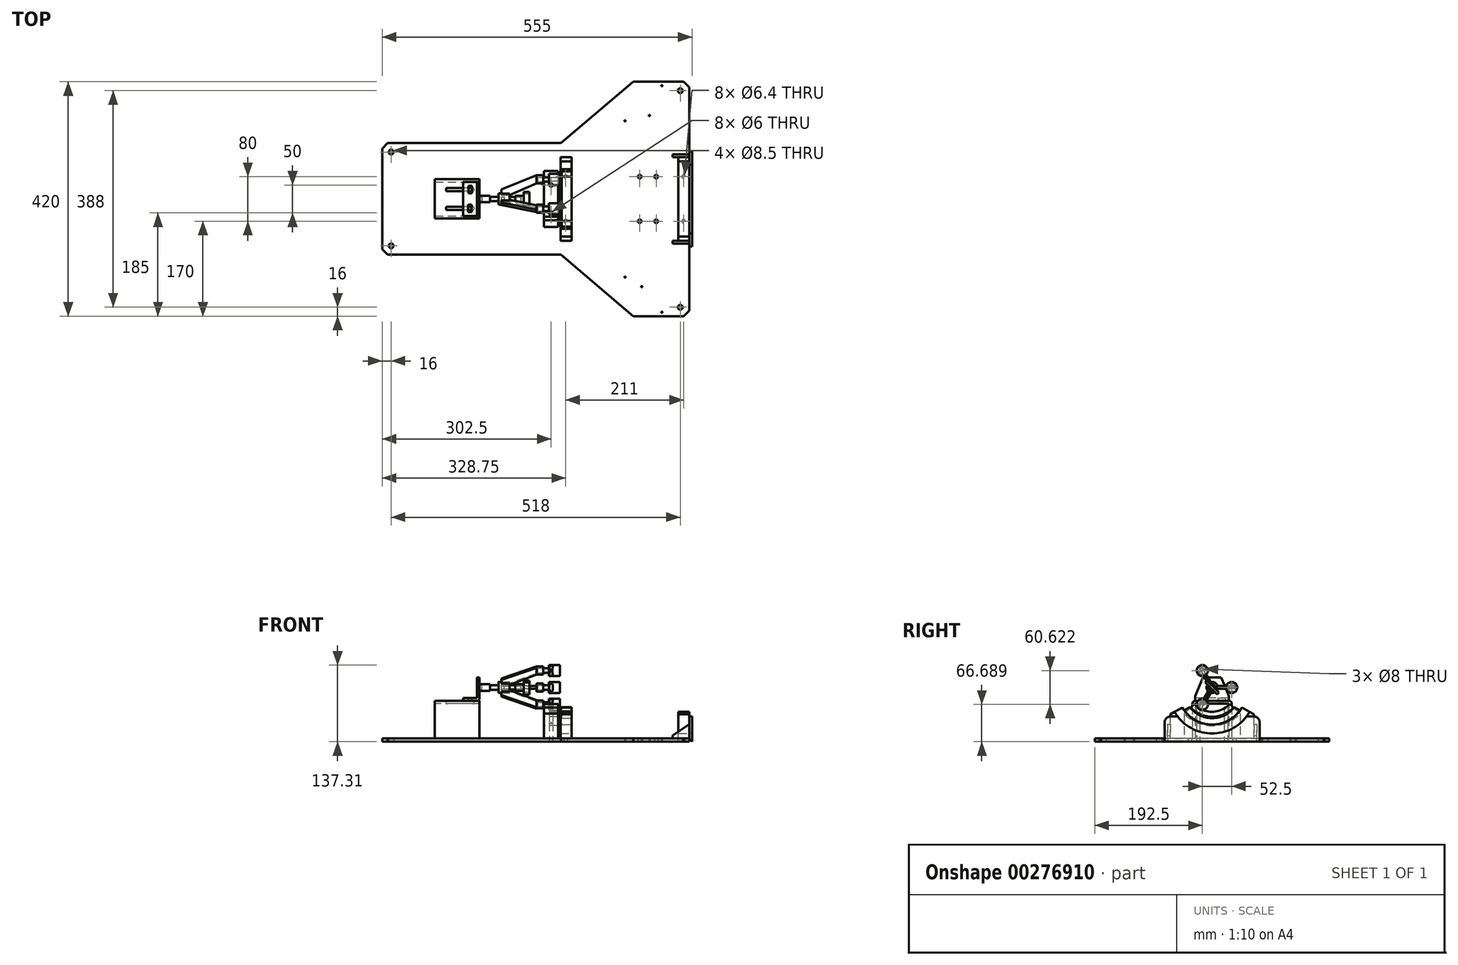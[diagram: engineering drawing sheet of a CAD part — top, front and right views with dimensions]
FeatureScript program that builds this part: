
annotation { "Feature Type Name" : "Feature", "Feature Type Description" : "" }
export const myFeature = defineFeature(function(context is Context, id is Id, definition is map)
    precondition{}
    {
        {
            var Q0;
            Q0=qCreatedBy(makeId("Top.planeOp"),FACE);
            var sketch = newSketch(context, id + "F0", { "sketchPlane" : qUnion([Q0])});
            skLineSegment(sketch, "E0.right", {"start": v(230, 200) * mm, "end": v(230, -200) * mm});
            skLineSegment(sketch, "E1", {"start": v(-320, 0) * mm, "end": v(230, 0) * mm, "construction": true});
            skCircle(sketch, "E2", {"center": v(8.75, 40) * mm, "radius": 3.2 * mm});
            skCircle(sketch, "E3", {"center": v(8.75, -40) * mm, "radius": 3.2 * mm});
            skCircle(sketch, "E4", {"center": v(115, -140) * mm, "radius": 1 * mm});
            skCircle(sketch, "E5", {"center": v(145, -157) * mm, "radius": 1 * mm});
            skCircle(sketch, "E6", {"center": v(181, -203) * mm, "radius": 1 * mm});
            skLineSegment(sketch, "E7", {"start": v(0, 0) * mm, "end": v(0, -188.14) * mm, "construction": true});
            skCircle(sketch, "E8", {"center": v(115, 140) * mm, "radius": 1 * mm});
            skCircle(sketch, "E9", {"center": v(158.66, 149.43) * mm, "radius": 1 * mm});
            skCircle(sketch, "E10", {"center": v(181, 203) * mm, "radius": 1 * mm});
            skLineSegment(sketch, "E11.0", {"start": v(-320, -50) * mm, "end": v(270, -50) * mm, "construction": true});
            skLineSegment(sketch, "E12.0", {"start": v(-320, 50) * mm, "end": v(270, 50) * mm, "construction": true});
            skLineSegment(sketch, "E13", {"start": v(-310, 100) * mm, "end": v(0, 100) * mm});
            skLineSegment(sketch, "E14", {"start": v(0, 100) * mm, "end": v(130, 210) * mm});
            skLineSegment(sketch, "E15", {"start": v(130, 210) * mm, "end": v(220, 210) * mm});
            skLineSegment(sketch, "E16", {"start": v(-310, -100) * mm, "end": v(0, -100) * mm});
            skLineSegment(sketch, "E17", {"start": v(0, -100) * mm, "end": v(130, -210) * mm});
            skLineSegment(sketch, "E18", {"start": v(-320, -90) * mm, "end": v(-320, 90) * mm});
            skLineSegment(sketch, "E19", {"start": v(130, -210) * mm, "end": v(220, -210) * mm});
            skLineSegment(sketch, "E20", {"start": v(8.75, 40) * mm, "end": v(230, 40) * mm, "construction": true});
            skCircle(sketch, "E21", {"center": v(141.25, 40) * mm, "radius": 3.2 * mm});
            skCircle(sketch, "E22", {"center": v(170.75, 40) * mm, "radius": 3.2 * mm});
            skCircle(sketch, "E23", {"center": v(219.75, 40) * mm, "radius": 3.2 * mm});
            skCircle(sketch, "E24", {"center": v(141.25, -40) * mm, "radius": 3.2 * mm});
            skCircle(sketch, "E25", {"center": v(170.75, -40) * mm, "radius": 3.2 * mm});
            skCircle(sketch, "E26", {"center": v(219.75, -40) * mm, "radius": 3.2 * mm});
            skLineSegment(sketch, "E27", {"start": v(-320, 90) * mm, "end": v(-310, 100) * mm});
            skLineSegment(sketch, "E28", {"start": v(-320, -90) * mm, "end": v(-310, -100) * mm});
            skLineSegment(sketch, "E29", {"start": v(220, -210) * mm, "end": v(230, -200) * mm});
            skLineSegment(sketch, "E30", {"start": v(220, 210) * mm, "end": v(230, 200) * mm});
            skPoint(sketch, "E31.orphan", {"position": v(-320, 100) * mm});
            skPoint(sketch, "E32.orphan", {"position": v(-320, -100) * mm});
            skPoint(sketch, "E33.orphan", {"position": v(230, -210) * mm});
            skPoint(sketch, "E34.orphan", {"position": v(230, 210) * mm});
            skSolve(sketch);
        }
        {
            var Q0;
            Q0=makeQuery(id+"F0.imprint","IMPRINT",FACE,{"disambiguationData":[TD([[makeQuery(id+"F0.imprint","IMPRINT",EDGE,{"derivedFrom":sQuery(id+"F0.wireOp",EDGE,"E0.right")}),-1.0]])]});
            extrude(context, id + "F1", {"entities" : qUnion([Q0]), "depth" : 6 * mm});
        }
        {
            var Q0;
            Q0=makeQuery(id+"F1.opExtrude","CAP_FACE",FACE,{"disambiguationData":[OSD([sQuery(id+"F0.wireOp",EDGE,"E0.right"),sQuery(id+"F0.wireOp",EDGE,"E2"),sQuery(id+"F0.wireOp",EDGE,"E3"),sQuery(id+"F0.wireOp",EDGE,"E4"),sQuery(id+"F0.wireOp",EDGE,"E5"),sQuery(id+"F0.wireOp",EDGE,"E6"),sQuery(id+"F0.wireOp",EDGE,"E8"),sQuery(id+"F0.wireOp",EDGE,"E9"),sQuery(id+"F0.wireOp",EDGE,"E10"),sQuery(id+"F0.wireOp",EDGE,"E13"),sQuery(id+"F0.wireOp",EDGE,"E14"),sQuery(id+"F0.wireOp",EDGE,"E15"),sQuery(id+"F0.wireOp",EDGE,"E16"),sQuery(id+"F0.wireOp",EDGE,"E17"),sQuery(id+"F0.wireOp",EDGE,"E18"),sQuery(id+"F0.wireOp",EDGE,"E19"),sQuery(id+"F0.wireOp",EDGE,"E21"),sQuery(id+"F0.wireOp",EDGE,"E22"),sQuery(id+"F0.wireOp",EDGE,"E23"),sQuery(id+"F0.wireOp",EDGE,"E24"),sQuery(id+"F0.wireOp",EDGE,"E25"),sQuery(id+"F0.wireOp",EDGE,"E26"),sQuery(id+"F0.wireOp",EDGE,"E27"),sQuery(id+"F0.wireOp",EDGE,"E28"),sQuery(id+"F0.wireOp",EDGE,"E29"),sQuery(id+"F0.wireOp",EDGE,"E30")])],"isStart":false});
            cPlane(context, id + "F2", {"entities" : qUnion([Q0]), "cplaneType" : CPlaneType.OFFSET, "offset" : 67 * mm, "width" : 150 * mm, "height" : 150 * mm});
        }
        {
            var Q0;
            Q0=qCreatedBy(id+"F2.planeOp",FACE);
            var sketch = newSketch(context, id + "F3", { "sketchPlane" : qUnion([Q0])});
            skLineSegment(sketch, "E35.bottom", {"start": v(-175.1, 30.25) * mm, "end": v(-145.6, 30.25) * mm});
            skLineSegment(sketch, "E35.top", {"start": v(-175.1, -30.25) * mm, "end": v(-145.6, -30.25) * mm});
            skLineSegment(sketch, "E35.left", {"start": v(-175.1, 30.25) * mm, "end": v(-175.1, -30.25) * mm});
            skLineSegment(sketch, "E35.right", {"start": v(-145.6, 30.25) * mm, "end": v(-145.6, -30.25) * mm});
            skLineSegment(sketch, "E36", {"start": v(0, 0) * mm, "end": v(-175.1, 0) * mm, "construction": true});
            skLineSegment(sketch, "E37.bottom", {"start": v(-166.1, -23.38) * mm, "end": v(-160.1, -23.38) * mm});
            skLineSegment(sketch, "E37.top", {"start": v(-166.1, -10.38) * mm, "end": v(-160.1, -10.38) * mm});
            skLineSegment(sketch, "E37.left", {"start": v(-166.1, -23.38) * mm, "end": v(-166.1, -10.38) * mm});
            skLineSegment(sketch, "E37.right", {"start": v(-160.1, -23.38) * mm, "end": v(-160.1, -10.38) * mm});
            skLineSegment(sketch, "E38.bottom", {"start": v(-165.48, 10.38) * mm, "end": v(-159.48, 10.38) * mm});
            skLineSegment(sketch, "E38.top", {"start": v(-165.48, 23.38) * mm, "end": v(-159.48, 23.38) * mm});
            skLineSegment(sketch, "E38.left", {"start": v(-165.48, 10.38) * mm, "end": v(-165.48, 23.38) * mm});
            skLineSegment(sketch, "E38.right", {"start": v(-159.48, 10.38) * mm, "end": v(-159.48, 23.38) * mm});
            skSolve(sketch);
        }
        {
            var Q0;
            Q0=makeQuery(id+"F3.imprint","IMPRINT",FACE,{"disambiguationData":[TD([[makeQuery(id+"F3.imprint","IMPRINT",EDGE,{"derivedFrom":sQuery(id+"F3.wireOp",EDGE,"E35.bottom")}),-1.0]])]});
            extrude(context, id + "F4", {"entities" : qUnion([Q0]), "depth" : 5 * mm});
        }
        {
            var Q0;
            Q0=makeQuery(id+"F4.opExtrude","SWEPT_FACE",FACE,{"disambiguationData":[OSD([sQuery(id+"F3.wireOp",EDGE,"E35.right")])]});
            var sketch = newSketch(context, id + "F5", { "sketchPlane" : qUnion([Q0])});
            skLineSegment(sketch, "E39.0", {"start": v(30.25, 73) * mm, "end": v(-30.25, 73) * mm});
            skLineSegment(sketch, "E39.1", {"start": v(-30.25, 78) * mm, "end": v(-30.25, 73) * mm});
            skLineSegment(sketch, "E39.2", {"start": v(30.25, 78) * mm, "end": v(30.25, 73) * mm});
            skLineSegment(sketch, "E40", {"start": v(-30.25, 78) * mm, "end": v(-30.25, 81.7) * mm});
            skLineSegment(sketch, "E41", {"start": v(-30.25, 81.7) * mm, "end": v(-16.23, 115) * mm});
            skLineSegment(sketch, "E42", {"start": v(-16.23, 115) * mm, "end": v(16.23, 115) * mm});
            skLineSegment(sketch, "E43", {"start": v(16.23, 115) * mm, "end": v(30.25, 81.7) * mm});
            skLineSegment(sketch, "E44", {"start": v(30.25, 81.7) * mm, "end": v(30.25, 78) * mm});
            skLineSegment(sketch, "E45", {"start": v(0, 115) * mm, "end": v(0, 78) * mm, "construction": true});
            skCircle(sketch, "E46", {"center": v(0, 97) * mm, "radius": 6 * mm, "construction": true});
            skSolve(sketch);
        }
        {
            var Q0;
            Q0=makeQuery(id+"F5.imprint","IMPRINT",FACE,{"disambiguationData":[TD([[makeQuery(id+"F5.imprint","IMPRINT",EDGE,{"derivedFrom":sQuery(id+"F5.wireOp",EDGE,"E40")}),-1.0]])]});
            extrude(context, id + "F6", {"entities" : qUnion([Q0]), "operationType" : NewBodyOperationType.ADD, "oppositeDirection" : true, "depth" : 5 * mm});
        }
        {
            var Q0;
            Q0=makeQuery(id+"F4.opExtrude","CAP_EDGE",EDGE,{"disambiguationData":[OSD([sQuery(id+"F3.wireOp",EDGE,"E35.right")])],"isStart":true});
            fillet(context, id + "F7", {"entities" : qUnion([Q0]), "radius" : 5 * mm, "tangentPropagation" : true, "allowEdgeOverflow" : false});
        }
        {
            var Q0;
            Q0=makeQuery(id+"F5.imprint","IMPRINT",FACE,{"disambiguationData":[TD([[makeQuery(id+"F5.imprint","IMPRINT",EDGE,{"derivedFrom":sQuery(id+"F5.wireOp",EDGE,"E40")}),-1.0]])]});
            var sketch = newSketch(context, id + "F8", { "sketchPlane" : qUnion([Q0])});
            skCircle(sketch, "E47.0", {"center": v(0, 97) * mm, "radius": 6 * mm});
            skCircle(sketch, "E48", {"center": v(0, 97) * mm, "radius": 4 * mm});
            skSolve(sketch);
        }
        {
            var Q0;
            Q0=makeQuery(id+"F8.imprint","IMPRINT",FACE,{"disambiguationData":[TD([[makeQuery(id+"F8.imprint","IMPRINT",EDGE,{"derivedFrom":sQuery(id+"F8.wireOp",EDGE,"E47.0")}),1.0]])]});
            var Q1;
            Q1=sQuery(id+"F8.wireOp",EDGE,"E47.0");
            extrude(context, id + "F9", {"entities" : qUnion([Q0]), "surfaceEntities" : qUnion([Q1]), "depth" : 19 * mm});
        }
        {
            var Q0;
            Q0=makeQuery(id+"F9.opExtrude","CAP_FACE",FACE,{"disambiguationData":[OSD([sQuery(id+"F8.wireOp",EDGE,"E47.0"),sQuery(id+"F8.wireOp",EDGE,"E48")])],"isStart":false});
            var sketch = newSketch(context, id + "F10", { "sketchPlane" : qUnion([Q0])});
            skCircle(sketch, "E49.0", {"center": v(0, 97) * mm, "radius": 4 * mm});
            skSolve(sketch);
        }
        {
            var Q0;
            Q0=makeQuery(id+"F10.imprint","IMPRINT",FACE,{"disambiguationData":[TD([[makeQuery(id+"F10.imprint","IMPRINT",EDGE,{"derivedFrom":sQuery(id+"F10.wireOp",EDGE,"E49.0")}),1.0]])]});
            extrude(context, id + "F11", {"entities" : qUnion([Q0]), "oppositeDirection" : true, "depth" : 15 * mm});
        }
        {
            var Q0;
            Q0=makeQuery(id+"F11.opExtrude","CAP_FACE",FACE,{"disambiguationData":[OSD([sQuery(id+"F10.wireOp",EDGE,"E49.0")])],"isStart":true});
            extrude(context, id + "F12", {"entities" : qUnion([Q0]), "operationType" : NewBodyOperationType.ADD, "depth" : 15 * mm});
        }
        {
            var Q0;
            Q0=makeQuery(id+"F12.opExtrude","CAP_FACE",FACE,{"disambiguationData":[OSD([sQuery(id+"F10.wireOp",EDGE,"E49.0")])],"isStart":false});
            var sketch = newSketch(context, id + "F13", { "sketchPlane" : qUnion([Q0])});
            skCircle(sketch, "E50", {"center": v(0, 97) * mm, "radius": 10 * mm});
            skSolve(sketch);
        }
        {
            var Q0;
            Q0=makeQuery(id+"F13.imprint","IMPRINT",FACE,{"disambiguationData":[TD([[makeQuery(id+"F13.imprint","IMPRINT",EDGE,{"derivedFrom":sQuery(id+"F13.wireOp",EDGE,"E50")}),1.0]])]});
            var Q1;
            Q1=makeQuery(id+"F13.imprint","IMPRINT",FACE,{"disambiguationData":[TD([[makeQuery(id+"F13.imprint","IMPRINT",EDGE,{"derivedFrom":makeQuery(id+"F12.opExtrude","CAP_EDGE",EDGE,{"disambiguationData":[OSD([sQuery(id+"F10.wireOp",EDGE,"E49.0")])],"isStart":false})}),1.0]])]});
            extrude(context, id + "F14", {"entities" : qUnion([Q0, Q1]), "operationType" : NewBodyOperationType.ADD, "depth" : 20 * mm});
        }
        {
            var Q0;
            Q0=makeQuery(id+"F14.opExtrude","CAP_FACE",FACE,{"disambiguationData":[OSD([sQuery(id+"F13.wireOp",EDGE,"E50")])],"isStart":false});
            var sketch = newSketch(context, id + "F15", { "sketchPlane" : qUnion([Q0])});
            skCircle(sketch, "E51", {"center": v(0, 97) * mm, "radius": 4 * mm});
            skLineSegment(sketch, "E52", {"start": v(0, 97) * mm, "end": v(10, 97) * mm, "construction": true});
            skLineSegment(sketch, "E53", {"start": v(0, 97) * mm, "end": v(-5, 88.34) * mm, "construction": true});
            skLineSegment(sketch, "E54", {"start": v(0, 97) * mm, "end": v(-5, 105.66) * mm, "construction": true});
            skLineSegment(sketch, "E55", {"start": v(9.68, 94.5) * mm, "end": v(7, 94.5) * mm});
            skLineSegment(sketch, "E56", {"start": v(7, 94.5) * mm, "end": v(7, 99.5) * mm});
            skLineSegment(sketch, "E57", {"start": v(7, 99.5) * mm, "end": v(9.68, 99.5) * mm});
            skLineSegment(sketch, "E58", {"start": v(-7, 89.86) * mm, "end": v(-5.67, 92.19) * mm});
            skLineSegment(sketch, "E59", {"start": v(-5.67, 92.19) * mm, "end": v(-1.33, 89.69) * mm});
            skLineSegment(sketch, "E60", {"start": v(-1.33, 89.69) * mm, "end": v(-2.68, 87.36) * mm});
            skLineSegment(sketch, "E61", {"start": v(-2.68, 106.64) * mm, "end": v(-1.33, 104.31) * mm});
            skLineSegment(sketch, "E62", {"start": v(-1.33, 104.31) * mm, "end": v(-5.67, 101.81) * mm});
            skLineSegment(sketch, "E63", {"start": v(-5.67, 101.81) * mm, "end": v(-7, 104.14) * mm});
            skSolve(sketch);
        }
        {
            var Q0;
            Q0=makeQuery(id+"F15.imprint","IMPRINT",FACE,{"disambiguationData":[TD([[makeQuery(id+"F15.imprint","IMPRINT",EDGE,{"derivedFrom":sQuery(id+"F15.wireOp",EDGE,"E51")}),1.0]])]});
            extrude(context, id + "F16", {"entities" : qUnion([Q0]), "operationType" : NewBodyOperationType.REMOVE, "oppositeDirection" : true, "depth" : 15 * mm});
        }
        {
            var Q0;
            {var subQ0=sQuery(id+"F15.wireOp",EDGE,"E61");Q0=makeQuery(id+"F15.imprint","IMPRINT",FACE,{"disambiguationData":[TD([[makeQuery(id+"F15.imprint","IMPRINT",EDGE,{"derivedFrom":subQ0}),-1.0]])]});}
            var Q1;
            {var subQ0=sQuery(id+"F15.wireOp",EDGE,"E58");Q1=makeQuery(id+"F15.imprint","IMPRINT",FACE,{"disambiguationData":[TD([[makeQuery(id+"F15.imprint","IMPRINT",EDGE,{"derivedFrom":subQ0}),-1.0]])]});}
            var Q2;
            {var subQ0=sQuery(id+"F15.wireOp",EDGE,"E55");Q2=makeQuery(id+"F15.imprint","IMPRINT",FACE,{"disambiguationData":[TD([[makeQuery(id+"F15.imprint","IMPRINT",EDGE,{"derivedFrom":subQ0}),-1.0]])]});}
            extrude(context, id + "F17", {"entities" : qUnion([Q0, Q1, Q2]), "operationType" : NewBodyOperationType.REMOVE, "oppositeDirection" : true, "depth" : 15 * mm});
        }
        {
            var Q0;
            Q0=makeQuery(id+"F14.opExtrude","CAP_FACE",FACE,{"disambiguationData":[OSD([sQuery(id+"F13.wireOp",EDGE,"E50")])],"isStart":false});
            var sketch = newSketch(context, id + "F18", { "sketchPlane" : qUnion([Q0])});
            skCircle(sketch, "E64", {"center": v(0, 97) * mm, "radius": 4 * mm});
            skSolve(sketch);
        }
        {
            var Q0;
            Q0=makeQuery(id+"F18.imprint","IMPRINT",FACE,{"disambiguationData":[TD([[makeQuery(id+"F18.imprint","IMPRINT",EDGE,{"derivedFrom":sQuery(id+"F18.wireOp",EDGE,"E64")}),1.0]])]});
            extrude(context, id + "F19", {"entities" : qUnion([Q0]), "oppositeDirection" : true, "depth" : 10 * mm});
        }
        {
            var Q0;
            Q0=makeQuery(id+"F19.opExtrude","CAP_FACE",FACE,{"disambiguationData":[OSD([sQuery(id+"F18.wireOp",EDGE,"E64")])],"isStart":true});
            extrude(context, id + "F20", {"entities" : qUnion([Q0]), "operationType" : NewBodyOperationType.ADD, "depth" : 20 * mm});
        }
        {
            var Q0;
            Q0=makeQuery(id+"F20.opExtrude","CAP_FACE",FACE,{"disambiguationData":[OSD([sQuery(id+"F18.wireOp",EDGE,"E64")])],"isStart":false});
            cPlane(context, id + "F21", {"entities" : qUnion([Q0]), "cplaneType" : CPlaneType.OFFSET, "offset" : 10 * mm, "oppositeDirection" : true, "width" : 150 * mm, "height" : 150 * mm});
        }
        {
            var Q0;
            Q0=qCreatedBy(id+"F21.planeOp",FACE);
            var sketch = newSketch(context, id + "F22", { "sketchPlane" : qUnion([Q0])});
            skLineSegment(sketch, "E65.0", {"start": v(0, 115) * mm, "end": v(0, 78) * mm, "construction": true});
            skCircle(sketch, "E66.0", {"center": v(0, 97) * mm, "radius": 4 * mm, "construction": true});
            skCircle(sketch, "E67", {"center": v(0, 97) * mm, "radius": 6 * mm});
            skSolve(sketch);
        }
        {
            var Q0;
            Q0=makeQuery(id+"F22.imprint","IMPRINT",FACE,{"disambiguationData":[TD([[makeQuery(id+"F22.imprint","IMPRINT",EDGE,{"derivedFrom":sQuery(id+"F22.wireOp",EDGE,"E67")}),1.0]])]});
            extrude(context, id + "F23", {"entities" : qUnion([Q0]), "depth" : 15 * mm});
        }
        {
            var Q0;
            Q0=makeQuery(id+"F23.opExtrude","CAP_FACE",FACE,{"disambiguationData":[OSD([sQuery(id+"F22.wireOp",EDGE,"E67")])],"isStart":false});
            var sketch = newSketch(context, id + "F24", { "sketchPlane" : qUnion([Q0])});
            skLineSegment(sketch, "E68", {"start": v(0, 103) * mm, "end": v(0, 91) * mm, "construction": true});
            skLineSegment(sketch, "E69.bottom", {"start": v(-2.5, 112) * mm, "end": v(2.5, 112) * mm});
            skLineSegment(sketch, "E69.top", {"start": v(-2.5, 82) * mm, "end": v(2.5, 82) * mm});
            skLineSegment(sketch, "E69.left", {"start": v(-2.5, 112) * mm, "end": v(-2.5, 82) * mm});
            skLineSegment(sketch, "E69.right", {"start": v(2.5, 112) * mm, "end": v(2.5, 82) * mm});
            skLineSegment(sketch, "E70", {"start": v(0, 97) * mm, "end": v(2.5, 97) * mm, "construction": true});
            skSolve(sketch);
        }
        {
            var Q0;
            {var subQ0=sQuery(id+"F24.wireOp",EDGE,"E69.bottom");Q0=makeQuery(id+"F24.imprint","IMPRINT",FACE,{"disambiguationData":[TD([[makeQuery(id+"F24.imprint","IMPRINT",EDGE,{"derivedFrom":subQ0}),-1.0]])]});}
            var Q1;
            {var subQ0=sQuery(id+"F24.wireOp",EDGE,"E69.left");var subQ1=makeQuery(id+"F23.opExtrude","CAP_EDGE",EDGE,{"disambiguationData":[OSD([sQuery(id+"F22.wireOp",EDGE,"E67")])],"isStart":false});var subQ2=makeQuery(id+"F24.imprint","INTERSECT",VERTEX,{"disambiguationData":[OD(0.0)],"derivedFrom":[subQ1,subQ0]});Q1=makeQuery(id+"F24.imprint","IMPRINT",FACE,{"disambiguationData":[TD([[makeQuery(id+"F24.imprint","IMPRINT",EDGE,{"disambiguationData":[TD([[subQ2,-1.0]])],"derivedFrom":subQ0}),1.0]])]});}
            var Q2;
            {var subQ0=sQuery(id+"F24.wireOp",EDGE,"E69.top");Q2=makeQuery(id+"F24.imprint","IMPRINT",FACE,{"disambiguationData":[TD([[makeQuery(id+"F24.imprint","IMPRINT",EDGE,{"derivedFrom":subQ0}),1.0]])]});}
            extrude(context, id + "F25", {"entities" : qUnion([Q0, Q1, Q2]), "operationType" : NewBodyOperationType.ADD, "depth" : 10 * mm});
        }
        {
            var Q0;
            Q0=makeQuery(id+"F23.opExtrude","SWEPT_BODY",BODY,{"disambiguationData":[OSD([sQuery(id+"F22.wireOp",EDGE,"E67")])]});
            var Q1;
            {var subQ0=sQuery(id+"F18.wireOp",EDGE,"E64");Q1=makeQuery(id+"F20.boolean.opBoolean","MERGE",FACE,{"derivedFrom":[makeQuery(id+"F19.opExtrude","SWEPT_FACE",FACE,{"disambiguationData":[OSD([subQ0])]}),makeQuery(id+"F20.opExtrude","SWEPT_FACE",FACE,{"disambiguationData":[OSD([subQ0])]})]});}
            transform(context, id + "F26", {"entities" : qUnion([Q0]), "transformType" : TransformType.ROTATION, "transformAxis" : qUnion([Q1]), "angle" : 45 * degree, "makeCopy" : false});
        }
        {
            var Q0;
            Q0=makeQuery(id+"F25.opExtrude","CAP_FACE",FACE,{"disambiguationData":[OSD([sQuery(id+"F24.wireOp",EDGE,"E69.bottom"),sQuery(id+"F24.wireOp",EDGE,"E69.top"),sQuery(id+"F24.wireOp",EDGE,"E69.left"),sQuery(id+"F24.wireOp",EDGE,"E69.right")])],"isStart":false});
            cPlane(context, id + "F27", {"entities" : qUnion([Q0]), "cplaneType" : CPlaneType.OFFSET, "offset" : 55 * mm, "width" : 150 * mm, "height" : 150 * mm});
        }
        {
            var Q0;
            Q0=qCreatedBy(id+"F27.planeOp",FACE);
            var sketch = newSketch(context, id + "F28", { "sketchPlane" : qUnion([Q0])});
            skCircle(sketch, "E71", {"center": v(0, 97) * mm, "radius": 43.5 * mm, "construction": true});
            skCircle(sketch, "E72", {"center": v(0, 97) * mm, "radius": 35 * mm, "construction": true});
            skLineSegment(sketch, "E73", {"start": v(0, 97) * mm, "end": v(43.5, 97) * mm, "construction": true});
            skLineSegment(sketch, "E74", {"start": v(0, 97) * mm, "end": v(-21.75, 59.33) * mm, "construction": true});
            skLineSegment(sketch, "E75", {"start": v(0, 97) * mm, "end": v(-21.75, 134.67) * mm, "construction": true});
            skCircle(sketch, "E76", {"center": v(-17.5, 66.69) * mm, "radius": 10 * mm});
            skCircle(sketch, "E77", {"center": v(35, 97) * mm, "radius": 10 * mm});
            skCircle(sketch, "E78", {"center": v(-17.5, 127.31) * mm, "radius": 10 * mm});
            skSolve(sketch);
        }
        {
            var Q0;
            Q0=makeQuery(id+"F28.imprint","IMPRINT",FACE,{"disambiguationData":[TD([[makeQuery(id+"F28.imprint","IMPRINT",EDGE,{"derivedFrom":sQuery(id+"F28.wireOp",EDGE,"E78")}),1.0]])]});
            var Q1;
            Q1=makeQuery(id+"F28.imprint","IMPRINT",FACE,{"disambiguationData":[TD([[makeQuery(id+"F28.imprint","IMPRINT",EDGE,{"derivedFrom":sQuery(id+"F28.wireOp",EDGE,"E77")}),1.0]])]});
            var Q2;
            Q2=makeQuery(id+"F28.imprint","IMPRINT",FACE,{"disambiguationData":[TD([[makeQuery(id+"F28.imprint","IMPRINT",EDGE,{"derivedFrom":sQuery(id+"F28.wireOp",EDGE,"E76")}),1.0]])]});
            extrude(context, id + "F29", {"entities" : qUnion([Q0, Q1, Q2]), "oppositeDirection" : true, "depth" : 20 * mm});
        }
        {
            var Q0;
            Q0=makeQuery(id+"F29.opExtrude","CAP_FACE",FACE,{"disambiguationData":[OSD([sQuery(id+"F28.wireOp",EDGE,"E78")])],"isStart":false});
            var sketch = newSketch(context, id + "F30", { "sketchPlane" : qUnion([Q0])});
            skCircle(sketch, "E79", {"center": v(17.5, 127.31) * mm, "radius": 4 * mm});
            skCircle(sketch, "E80", {"center": v(17.5, 66.69) * mm, "radius": 4 * mm});
            skCircle(sketch, "E81", {"center": v(-35, 97) * mm, "radius": 4 * mm});
            skSolve(sketch);
        }
        {
            var Q0;
            Q0=makeQuery(id+"F30.imprint","IMPRINT",FACE,{"disambiguationData":[TD([[makeQuery(id+"F30.imprint","IMPRINT",EDGE,{"derivedFrom":sQuery(id+"F30.wireOp",EDGE,"E80")}),1.0]])]});
            var Q1;
            Q1=makeQuery(id+"F30.imprint","IMPRINT",FACE,{"disambiguationData":[TD([[makeQuery(id+"F30.imprint","IMPRINT",EDGE,{"derivedFrom":sQuery(id+"F30.wireOp",EDGE,"E81")}),1.0]])]});
            var Q2;
            Q2=makeQuery(id+"F30.imprint","IMPRINT",FACE,{"disambiguationData":[TD([[makeQuery(id+"F30.imprint","IMPRINT",EDGE,{"derivedFrom":sQuery(id+"F30.wireOp",EDGE,"E79")}),1.0]])]});
            extrude(context, id + "F31", {"entities" : qUnion([Q0, Q1, Q2]), "depth" : 20 * mm});
        }
        {
            var Q0;
            Q0=makeQuery(id+"F31.opExtrude","CAP_FACE",FACE,{"disambiguationData":[OSD([sQuery(id+"F30.wireOp",EDGE,"E79")])],"isStart":false});
            cPlane(context, id + "F32", {"entities" : qUnion([Q0]), "cplaneType" : CPlaneType.OFFSET, "offset" : 10 * mm, "oppositeDirection" : true, "width" : 150 * mm, "height" : 150 * mm});
        }
        {
            var Q0;
            Q0=qCreatedBy(id+"F32.planeOp",FACE);
            var sketch = newSketch(context, id + "F33", { "sketchPlane" : qUnion([Q0])});
            skCircle(sketch, "E82.0", {"center": v(17.5, 127.31) * mm, "radius": 4 * mm});
            skCircle(sketch, "E82.1", {"center": v(-35, 97) * mm, "radius": 4 * mm});
            skCircle(sketch, "E82.2", {"center": v(17.5, 66.69) * mm, "radius": 4 * mm});
            skCircle(sketch, "E83", {"center": v(17.5, 127.31) * mm, "radius": 7.2 * mm});
            skCircle(sketch, "E84", {"center": v(-35, 97) * mm, "radius": 7.2 * mm});
            skCircle(sketch, "E85", {"center": v(17.5, 66.69) * mm, "radius": 7.2 * mm});
            skSolve(sketch);
        }
        {
            var Q0;
            Q0=makeQuery(id+"F33.imprint","IMPRINT",FACE,{"disambiguationData":[TD([[makeQuery(id+"F33.imprint","IMPRINT",EDGE,{"derivedFrom":sQuery(id+"F33.wireOp",EDGE,"E82.0")}),-1.0]])]});
            var Q1;
            Q1=makeQuery(id+"F33.imprint","IMPRINT",FACE,{"disambiguationData":[TD([[makeQuery(id+"F33.imprint","IMPRINT",EDGE,{"derivedFrom":sQuery(id+"F33.wireOp",EDGE,"E82.2")}),-1.0]])]});
            var Q2;
            Q2=makeQuery(id+"F33.imprint","IMPRINT",FACE,{"disambiguationData":[TD([[makeQuery(id+"F33.imprint","IMPRINT",EDGE,{"derivedFrom":sQuery(id+"F33.wireOp",EDGE,"E82.1")}),-1.0]])]});
            extrude(context, id + "F34", {"entities" : qUnion([Q0, Q1, Q2]), "depth" : 12 * mm});
        }
        {
            var Q0;
            Q0=makeQuery(id+"F17.boolean.opBoolean","COPY",FACE,{"derivedFrom":makeQuery(id+"F17.opExtrude","SWEPT_FACE",FACE,{"disambiguationData":[OSD([sQuery(id+"F15.wireOp",EDGE,"E63")])]})});
            var sketch = newSketch(context, id + "F35", { "sketchPlane" : qUnion([Q0])});
            skLineSegment(sketch, "E86.0", {"start": v(106.6, 91) * mm, "end": v(91.6, 91) * mm});
            skLineSegment(sketch, "E87.0", {"start": v(106.6, 93.69) * mm, "end": v(106.6, 91) * mm});
            skLineSegment(sketch, "E88", {"start": v(106.6, 93.69) * mm, "end": v(106.6, 101) * mm});
            skLineSegment(sketch, "E89", {"start": v(106.6, 101) * mm, "end": v(43.6, 126.2) * mm});
            skLineSegment(sketch, "E90.0", {"start": v(43.6, 126.2) * mm, "end": v(43.6, 111.8) * mm});
            skLineSegment(sketch, "E91", {"start": v(43.6, 111.8) * mm, "end": v(91.6, 91) * mm});
            skSolve(sketch);
        }
        {
            var Q0;
            Q0=makeQuery(id+"F35.imprint","IMPRINT",FACE,{"disambiguationData":[TD([[makeQuery(id+"F35.imprint","IMPRINT",EDGE,{"derivedFrom":sQuery(id+"F35.wireOp",EDGE,"E88")}),1.0]])]});
            var Q1;
            Q1=makeQuery(id+"F35.imprint","IMPRINT",FACE,{"disambiguationData":[TD([[makeQuery(id+"F35.imprint","IMPRINT",EDGE,{"derivedFrom":sQuery(id+"F35.wireOp",EDGE,"E86.0")}),-1.0]])]});
            extrude(context, id + "F36", {"entities" : qUnion([Q0, Q1]), "depth" : 5 * mm});
        }
        {
            var Q0;
            Q0=makeQuery(id+"F36.opExtrude","SWEPT_BODY",BODY,{"disambiguationData":[OSD([sQuery(id+"F13.wireOp",EDGE,"E50"),sQuery(id+"F15.wireOp",EDGE,"E63"),sQuery(id+"F35.wireOp",EDGE,"E88"),sQuery(id+"F35.wireOp",EDGE,"E89"),sQuery(id+"F35.wireOp",EDGE,"E90.0"),sQuery(id+"F35.wireOp",EDGE,"E91")])]});
            var Q1;
            Q1=makeQuery(id+"F14.opExtrude","SWEPT_FACE",FACE,{"disambiguationData":[OSD([sQuery(id+"F13.wireOp",EDGE,"E50")])]});
            transform(context, id + "F37", {"entities" : qUnion([Q0]), "transformType" : TransformType.ROTATION, "transformAxis" : qUnion([Q1]), "angle" : 120 * degree, "makeCopy" : true});
        }
        {
            var Q0;
            Q0=makeQuery(id+"F36.opExtrude","SWEPT_BODY",BODY,{"disambiguationData":[OSD([sQuery(id+"F13.wireOp",EDGE,"E50"),sQuery(id+"F15.wireOp",EDGE,"E63"),sQuery(id+"F35.wireOp",EDGE,"E88"),sQuery(id+"F35.wireOp",EDGE,"E89"),sQuery(id+"F35.wireOp",EDGE,"E90.0"),sQuery(id+"F35.wireOp",EDGE,"E91")])]});
            var Q1;
            Q1=makeQuery(id+"F14.opExtrude","SWEPT_FACE",FACE,{"disambiguationData":[OSD([sQuery(id+"F13.wireOp",EDGE,"E50")])]});
            transform(context, id + "F38", {"entities" : qUnion([Q0]), "transformType" : TransformType.ROTATION, "transformAxis" : qUnion([Q1]), "angle" : 120 * degree, "oppositeDirection" : true, "makeCopy" : true});
        }
        {
            var Q0;
            Q0=makeQuery(id+"F1.opExtrude","SWEPT_FACE",FACE,{"disambiguationData":[OSD([sQuery(id+"F0.wireOp",EDGE,"E0.right")])]});
            var sketch = newSketch(context, id + "F39", { "sketchPlane" : qUnion([Q0])});
            skLineSegment(sketch, "E92.bottom", {"start": v(-75, 6) * mm, "end": v(75, 6) * mm});
            skLineSegment(sketch, "E92.left", {"start": v(-75, 6) * mm, "end": v(-75, 48.7) * mm});
            skLineSegment(sketch, "E92.right", {"start": v(75, 6) * mm, "end": v(75, 48.7) * mm});
            skLineSegment(sketch, "E93.trimOffspring", {"start": v(-67.12, 53.25) * mm, "end": v(-75, 48.7) * mm});
            skLineSegment(sketch, "E94.trimOffspring", {"start": v(67.12, 53.25) * mm, "end": v(75, 48.7) * mm});
            skLineSegment(sketch, "E95", {"start": v(0, 92) * mm, "end": v(0, 6) * mm, "construction": true});
            skPoint(sketch, "E95.endSnap0", {"position": v(0, -48.02) * mm});
            skLineSegment(sketch, "E96", {"start": v(0, 92) * mm, "end": v(75, 48.7) * mm, "construction": true});
            skArc(sketch, "E97", {"start": v(-67.12, 53.25) * mm, "mid": v(0, 14.5) * mm, "end": v(67.12, 53.25) * mm});
            skLineSegment(sketch, "E98", {"start": v(0, 6) * mm, "end": v(0, 14.5) * mm, "construction": true});
            skLineSegment(sketch, "E99.0", {"start": v(200, 6) * mm, "end": v(-200, 6) * mm, "construction": true});
            skLineSegment(sketch, "E100", {"start": v(0, 0) * mm, "end": v(0, 50) * mm, "construction": true});
            skSolve(sketch);
        }
        {
            var Q0;
            Q0=makeQuery(id+"F39.imprint","IMPRINT",FACE,{"disambiguationData":[TD([[makeQuery(id+"F39.imprint","IMPRINT",EDGE,{"derivedFrom":sQuery(id+"F39.wireOp",EDGE,"E92.bottom")}),-1.0]])]});
            extrude(context, id + "F40", {"entities" : qUnion([Q0]), "oppositeDirection" : true, "depth" : 19.5 * mm});
        }
        {
            var Q0;
            Q0=makeQuery(id+"F4.opExtrude","CAP_FACE",FACE,{"disambiguationData":[OSD([sQuery(id+"F3.wireOp",EDGE,"E35.bottom"),sQuery(id+"F3.wireOp",EDGE,"E35.top"),sQuery(id+"F3.wireOp",EDGE,"E35.left"),sQuery(id+"F3.wireOp",EDGE,"E35.right"),sQuery(id+"F3.wireOp",EDGE,"E37.bottom"),sQuery(id+"F3.wireOp",EDGE,"E37.top"),sQuery(id+"F3.wireOp",EDGE,"E37.left"),sQuery(id+"F3.wireOp",EDGE,"E37.right"),sQuery(id+"F3.wireOp",EDGE,"E38.bottom"),sQuery(id+"F3.wireOp",EDGE,"E38.top"),sQuery(id+"F3.wireOp",EDGE,"E38.left"),sQuery(id+"F3.wireOp",EDGE,"E38.right")])],"isStart":true});
            var sketch = newSketch(context, id + "F41", { "sketchPlane" : qUnion([Q0])});
            skLineSegment(sketch, "E101.0", {"start": v(-166.1, 23.38) * mm, "end": v(-166.1, 10.38) * mm, "construction": true});
            skLineSegment(sketch, "E102.0", {"start": v(-160.1, 23.38) * mm, "end": v(-160.1, 10.38) * mm, "construction": true});
            skLineSegment(sketch, "E103.0", {"start": v(-165.48, -10.38) * mm, "end": v(-165.48, -23.38) * mm, "construction": true});
            skLineSegment(sketch, "E104.0", {"start": v(-159.48, -10.38) * mm, "end": v(-159.48, -23.38) * mm, "construction": true});
            skLineSegment(sketch, "E105.0", {"start": v(-145.6, 30.25) * mm, "end": v(-145.6, -30.25) * mm});
            skLineSegment(sketch, "E105.1", {"start": v(-145.6, -30.25) * mm, "end": v(-145.6, 30.25) * mm, "construction": true});
            skLineSegment(sketch, "E106", {"start": v(-140.17, -30.25) * mm, "end": v(-140.17, 30.25) * mm});
            skLineSegment(sketch, "E107", {"start": v(-140.17, -30.25) * mm, "end": v(-225.6, -30.25) * mm});
            skLineSegment(sketch, "E108", {"start": v(-140.17, 30.25) * mm, "end": v(-225.6, 30.25) * mm});
            skPoint(sketch, "E108.endSnap0", {"position": v(-162.85, 30.25) * mm});
            skLineSegment(sketch, "E109", {"start": v(-140.17, 0) * mm, "end": v(-247.58, 0) * mm, "construction": true});
            skPoint(sketch, "E109.startSnap0", {"position": v(-145.6, 0) * mm});
            skPoint(sketch, "E109.endSnap0", {"position": v(-145.6, 0) * mm});
            skLineSegment(sketch, "E110", {"start": v(-159.48, -16.88) * mm, "end": v(-225.6, -16.88) * mm, "construction": true});
            skPoint(sketch, "E110.endSnap0", {"position": v(-159.48, -16.88) * mm});
            skLineSegment(sketch, "E111", {"start": v(-157.6, -19.88) * mm, "end": v(-203.6, -19.88) * mm});
            skLineSegment(sketch, "E112", {"start": v(-157.6, -13.88) * mm, "end": v(-203.6, -13.88) * mm});
            skLineSegment(sketch, "E113", {"start": v(-155.6, -17.88) * mm, "end": v(-155.6, -15.88) * mm});
            skPoint(sketch, "E114.visualSharp", {"position": v(-155.6, -19.88) * mm});
            skArc(sketch, "E114.filletArc", {"start": v(-157.6, -19.88) * mm, "mid": v(-156.18, -19.3) * mm, "end": v(-155.6, -17.88) * mm});
            skPoint(sketch, "E115.visualSharp", {"position": v(-155.6, -13.88) * mm});
            skArc(sketch, "E115.filletArc", {"start": v(-155.6, -15.88) * mm, "mid": v(-156.18, -14.47) * mm, "end": v(-157.6, -13.88) * mm});
            skLineSegment(sketch, "E116", {"start": v(-205.6, -15.88) * mm, "end": v(-205.6, -17.88) * mm});
            skPoint(sketch, "E117.visualSharp", {"position": v(-205.6, -19.88) * mm});
            skArc(sketch, "E117.filletArc", {"start": v(-205.6, -17.88) * mm, "mid": v(-205, -19.3) * mm, "end": v(-203.6, -19.88) * mm});
            skPoint(sketch, "E118.visualSharp", {"position": v(-205.6, -13.88) * mm});
            skArc(sketch, "E118.filletArc", {"start": v(-203.6, -13.88) * mm, "mid": v(-205, -14.47) * mm, "end": v(-205.6, -15.88) * mm});
            skLineSegment(sketch, "E119.bottom", {"start": v(-157.6, 13.88) * mm, "end": v(-203.6, 13.88) * mm});
            skLineSegment(sketch, "E119.top", {"start": v(-157.6, 19.88) * mm, "end": v(-203.6, 19.88) * mm});
            skLineSegment(sketch, "E119.left", {"start": v(-155.6, 15.88) * mm, "end": v(-155.6, 17.88) * mm});
            skLineSegment(sketch, "E119.right", {"start": v(-205.6, 15.88) * mm, "end": v(-205.6, 17.88) * mm});
            skPoint(sketch, "E120.visualSharp", {"position": v(-205.6, 13.88) * mm});
            skArc(sketch, "E120.filletArc", {"start": v(-205.6, 15.88) * mm, "mid": v(-205, 14.47) * mm, "end": v(-203.6, 13.88) * mm});
            skPoint(sketch, "E121.visualSharp", {"position": v(-205.6, 19.88) * mm});
            skArc(sketch, "E121.filletArc", {"start": v(-203.6, 19.88) * mm, "mid": v(-205, 19.3) * mm, "end": v(-205.6, 17.88) * mm});
            skPoint(sketch, "E122.visualSharp", {"position": v(-155.6, 19.88) * mm});
            skArc(sketch, "E122.filletArc", {"start": v(-155.6, 17.88) * mm, "mid": v(-156.18, 19.3) * mm, "end": v(-157.6, 19.88) * mm});
            skPoint(sketch, "E123.visualSharp", {"position": v(-155.6, 13.88) * mm});
            skArc(sketch, "E123.filletArc", {"start": v(-157.6, 13.88) * mm, "mid": v(-156.18, 14.47) * mm, "end": v(-155.6, 15.88) * mm});
            skLineSegment(sketch, "E124", {"start": v(-180.6, -19.88) * mm, "end": v(-180.6, 19.88) * mm, "construction": true});
            skLineSegment(sketch, "E125", {"start": v(-225.6, -30.25) * mm, "end": v(-225.6, 30.25) * mm});
            skSolve(sketch);
        }
        {
            var Q0;
            Q0=makeQuery(id+"F41.imprint","IMPRINT",FACE,{"disambiguationData":[TD([[makeQuery(id+"F41.imprint","IMPRINT",EDGE,{"derivedFrom":sQuery(id+"F41.wireOp",EDGE,"E116")}),-1.0]])]});
            var Q1;
            Q1=makeQuery(id+"F41.imprint","IMPRINT",FACE,{"disambiguationData":[TD([[makeQuery(id+"F41.imprint","IMPRINT",EDGE,{"derivedFrom":sQuery(id+"F41.wireOp",EDGE,"E113")}),-1.0]])]});
            var Q2;
            {var subQ5=makeQuery(id+"F4.opExtrude","CAP_EDGE",EDGE,{"disambiguationData":[OSD([sQuery(id+"F3.wireOp",EDGE,"E38.top")])],"isStart":true});Q2=makeQuery(id+"F41.imprint","IMPRINT",FACE,{"disambiguationData":[TD([[makeQuery(id+"F41.imprint","IMPRINT",EDGE,{"derivedFrom":subQ5}),1.0]])]});}
            var Q3;
            {var subQ5=makeQuery(id+"F4.opExtrude","CAP_EDGE",EDGE,{"disambiguationData":[OSD([sQuery(id+"F3.wireOp",EDGE,"E38.bottom")])],"isStart":true});Q3=makeQuery(id+"F41.imprint","IMPRINT",FACE,{"disambiguationData":[TD([[makeQuery(id+"F41.imprint","IMPRINT",EDGE,{"derivedFrom":subQ5}),-1.0]])]});}
            var Q4;
            {var subQ5=makeQuery(id+"F4.opExtrude","CAP_EDGE",EDGE,{"disambiguationData":[OSD([sQuery(id+"F3.wireOp",EDGE,"E37.top")])],"isStart":true});Q4=makeQuery(id+"F41.imprint","IMPRINT",FACE,{"disambiguationData":[TD([[makeQuery(id+"F41.imprint","IMPRINT",EDGE,{"derivedFrom":subQ5}),1.0]])]});}
            var Q5;
            {var subQ5=makeQuery(id+"F4.opExtrude","CAP_EDGE",EDGE,{"disambiguationData":[OSD([sQuery(id+"F3.wireOp",EDGE,"E37.bottom")])],"isStart":true});Q5=makeQuery(id+"F41.imprint","IMPRINT",FACE,{"disambiguationData":[TD([[makeQuery(id+"F41.imprint","IMPRINT",EDGE,{"derivedFrom":subQ5}),-1.0]])]});}
            var Q6;
            {var subQ0=sQuery(id+"F41.wireOp",EDGE,"E105.0");Q6=makeQuery(id+"F41.imprint","IMPRINT",FACE,{"disambiguationData":[TD([[makeQuery(id+"F41.imprint","IMPRINT",EDGE,{"derivedFrom":subQ0}),-1.0]])]});}
            extrude(context, id + "F42", {"entities" : qUnion([Q0, Q1, Q2, Q3, Q4, Q5, Q6]), "depth" : 5 * mm});
        }
        {
            var Q0;
            Q0=makeQuery(id+"F42.opExtrude","SWEPT_FACE",FACE,{"disambiguationData":[OSD([sQuery(id+"F41.wireOp",EDGE,"E108")])]});
            var sketch = newSketch(context, id + "F43", { "sketchPlane" : qUnion([Q0])});
            skLineSegment(sketch, "E126.0", {"start": v(-145.6, 73) * mm, "end": v(-225.6, 73) * mm});
            skLineSegment(sketch, "E127.0", {"start": v(-310, 6) * mm, "end": v(0, 6) * mm});
            skLineSegment(sketch, "E128", {"start": v(-145.6, 73) * mm, "end": v(-145.6, 6) * mm});
            skLineSegment(sketch, "E129", {"start": v(-225.6, 73) * mm, "end": v(-225.6, 6) * mm});
            skLineSegment(sketch, "E130.0", {"start": v(-145.6, 68) * mm, "end": v(-225.6, 68) * mm, "construction": true});
            skSolve(sketch);
        }
        {
            var Q0;
            {var subQ5=makeQuery(id+"F42.opExtrude","CAP_EDGE",EDGE,{"disambiguationData":[OSD([sQuery(id+"F41.wireOp",EDGE,"E108")])],"isStart":false});Q0=makeQuery(id+"F43.imprint","IMPRINT",FACE,{"disambiguationData":[TD([[makeQuery(id+"F43.imprint","IMPRINT",EDGE,{"derivedFrom":subQ5}),1.0]])]});}
            var Q1;
            {var subQ0=sQuery(id+"F43.wireOp",EDGE,"E126.0");Q1=makeQuery(id+"F43.imprint","IMPRINT",FACE,{"disambiguationData":[TD([[makeQuery(id+"F43.imprint","IMPRINT",EDGE,{"derivedFrom":subQ0}),1.0]])]});}
            extrude(context, id + "F44", {"entities" : qUnion([Q0, Q1]), "operationType" : NewBodyOperationType.ADD, "depth" : 5 * mm});
        }
        {
            var Q0;
            Q0=makeQuery(id+"F44.opExtrude","CAP_EDGE",EDGE,{"disambiguationData":[OSD([sQuery(id+"F43.wireOp",EDGE,"E126.0")])],"isStart":false});
            fillet(context, id + "F45", {"entities" : qUnion([Q0]), "radius" : 5 * mm, "tangentPropagation" : true, "allowEdgeOverflow" : false});
        }
        {
            var Q0;
            Q0=makeQuery(id+"F44.boolean.opBoolean","MERGE",FACE,{"derivedFrom":[makeQuery(id+"F6.boolean.opBoolean","MERGE",FACE,{"derivedFrom":[makeQuery(id+"F4.opExtrude","SWEPT_FACE",FACE,{"disambiguationData":[OSD([sQuery(id+"F3.wireOp",EDGE,"E35.bottom")])]}),makeQuery(id+"F6.opExtrude","SWEPT_FACE",FACE,{"disambiguationData":[OSD([sQuery(id+"F5.wireOp",EDGE,"E44")])]})]}),makeQuery(id+"F42.opExtrude","SWEPT_FACE",FACE,{"disambiguationData":[OSD([sQuery(id+"F41.wireOp",EDGE,"E107")])]})]});
            var sketch = newSketch(context, id + "F46", { "sketchPlane" : qUnion([Q0])});
            skLineSegment(sketch, "E131", {"start": v(225.6, 73) * mm, "end": v(145.6, 73) * mm});
            skLineSegment(sketch, "E132.0", {"start": v(310, 6) * mm, "end": v(0, 6) * mm});
            skLineSegment(sketch, "E133", {"start": v(145.6, 73) * mm, "end": v(145.6, 6) * mm});
            skLineSegment(sketch, "E134", {"start": v(225.6, 73) * mm, "end": v(225.6, 6) * mm});
            skSolve(sketch);
        }
        {
            var Q0;
            {var subQ5=makeQuery(id+"F42.opExtrude","CAP_EDGE",EDGE,{"disambiguationData":[OSD([sQuery(id+"F41.wireOp",EDGE,"E107")])],"isStart":false});Q0=makeQuery(id+"F46.imprint","IMPRINT",FACE,{"disambiguationData":[TD([[makeQuery(id+"F46.imprint","IMPRINT",EDGE,{"derivedFrom":subQ5}),-1.0]])]});}
            var Q1;
            {var subQ1=makeQuery(id+"F42.opExtrude","CAP_EDGE",EDGE,{"disambiguationData":[OSD([sQuery(id+"F41.wireOp",EDGE,"E107")])],"isStart":false});Q1=makeQuery(id+"F46.imprint","IMPRINT",FACE,{"disambiguationData":[TD([[makeQuery(id+"F46.imprint","IMPRINT",EDGE,{"derivedFrom":subQ1}),1.0]])]});}
            extrude(context, id + "F47", {"entities" : qUnion([Q0, Q1]), "operationType" : NewBodyOperationType.ADD, "depth" : 5 * mm});
        }
        {
            var Q0;
            Q0=makeQuery(id+"F47.opExtrude","CAP_EDGE",EDGE,{"disambiguationData":[OSD([sQuery(id+"F46.wireOp",EDGE,"E131")])],"isStart":false});
            fillet(context, id + "F48", {"entities" : qUnion([Q0]), "radius" : 5 * mm, "tangentPropagation" : true, "allowEdgeOverflow" : false});
        }
        {
            var Q0;
            Q0=makeQuery(id+"F40.opExtrude","CAP_FACE",FACE,{"disambiguationData":[OSD([sQuery(id+"F39.wireOp",EDGE,"E92.bottom"),sQuery(id+"F39.wireOp",EDGE,"E92.left"),sQuery(id+"F39.wireOp",EDGE,"E92.right"),sQuery(id+"F39.wireOp",EDGE,"E93.trimOffspring"),sQuery(id+"F39.wireOp",EDGE,"E94.trimOffspring"),sQuery(id+"F39.wireOp",EDGE,"E97")])],"isStart":true});
            var sketch = newSketch(context, id + "F49", { "sketchPlane" : qUnion([Q0])});
            skLineSegment(sketch, "E135.0", {"start": v(200, 0) * mm, "end": v(-200, 0) * mm});
            skArc(sketch, "E136.0", {"start": v(-67.12, 53.25) * mm, "mid": v(0, 14.5) * mm, "end": v(67.12, 53.25) * mm});
            skLineSegment(sketch, "E137", {"start": v(-75, 48.7) * mm, "end": v(-64.27, 48.7) * mm, "construction": true});
            skLineSegment(sketch, "E138", {"start": v(75, 48.7) * mm, "end": v(64.27, 48.7) * mm, "construction": true});
            skLineSegment(sketch, "E139", {"start": v(-85, 0) * mm, "end": v(-85, 35) * mm});
            skLineSegment(sketch, "E140", {"start": v(-75, 45) * mm, "end": v(-61.62, 45) * mm});
            skLineSegment(sketch, "E141", {"start": v(0, 0) * mm, "end": v(0, 14.5) * mm, "construction": true});
            skPoint(sketch, "E142.visualSharp", {"position": v(-85, 45) * mm});
            skArc(sketch, "E142.filletArc", {"start": v(-75, 45) * mm, "mid": v(-82.07, 42.07) * mm, "end": v(-85, 35) * mm});
            skLineSegment(sketch, "E143", {"start": v(-61.62, 45) * mm, "end": v(61.62, 45) * mm, "construction": true});
            skLineSegment(sketch, "E144", {"start": v(61.62, 45) * mm, "end": v(75, 45) * mm});
            skLineSegment(sketch, "E145", {"start": v(85, 0) * mm, "end": v(85, 35) * mm});
            skLineSegment(sketch, "E146", {"start": v(75, 45) * mm, "end": v(75, 45) * mm});
            skPoint(sketch, "E147.visualSharp", {"position": v(85, 45) * mm});
            skArc(sketch, "E147.filletArc", {"start": v(85, 35) * mm, "mid": v(82.07, 42.07) * mm, "end": v(75, 45) * mm});
            skSolve(sketch);
        }
        {
            var Q0;
            {var subQ2=sQuery(id+"F49.wireOp",EDGE,"E139");Q0=makeQuery(id+"F49.imprint","IMPRINT",FACE,{"disambiguationData":[TD([[makeQuery(id+"F49.imprint","IMPRINT",EDGE,{"derivedFrom":subQ2}),-1.0]])]});}
            var Q1;
            {var subQ1=sQuery(id+"F49.wireOp",EDGE,"E140");Q1=makeQuery(id+"F49.imprint","IMPRINT",FACE,{"disambiguationData":[TD([[makeQuery(id+"F49.imprint","IMPRINT",EDGE,{"derivedFrom":subQ1}),-1.0]])]});}
            extrude(context, id + "F50", {"entities" : qUnion([Q0, Q1]), "depth" : 5 * mm});
        }
        {
            var Q0;
            Q0=makeQuery(id+"F50.opExtrude","CAP_EDGE",EDGE,{"disambiguationData":[OSD([sQuery(id+"F49.wireOp",EDGE,"E135.0")])],"isStart":true});
            chamfer(context, id + "F51", {"entities" : qUnion([Q0]), "width" : 5 * mm, "tangentPropagation" : true});
        }
        {
            var Q0;
            Q0=makeQuery(id+"F40.opExtrude","SWEPT_FACE",FACE,{"disambiguationData":[OSD([sQuery(id+"F39.wireOp",EDGE,"E92.left")])]});
            var sketch = newSketch(context, id + "F52", { "sketchPlane" : qUnion([Q0])});
            skLineSegment(sketch, "E148", {"start": v(230, 6) * mm, "end": v(200, 6) * mm});
            skLineSegment(sketch, "E149", {"start": v(200, 6) * mm, "end": v(200, 11) * mm});
            skLineSegment(sketch, "E150", {"start": v(230, 6) * mm, "end": v(230, 31) * mm});
            skLineSegment(sketch, "E151", {"start": v(230, 31) * mm, "end": v(200, 11) * mm});
            skSolve(sketch);
        }
        {
            var Q0;
            {var subQ3=sQuery(id+"F52.wireOp",EDGE,"E149");Q0=makeQuery(id+"F52.imprint","IMPRINT",FACE,{"disambiguationData":[TD([[makeQuery(id+"F52.imprint","IMPRINT",EDGE,{"derivedFrom":subQ3}),-1.0]])]});}
            var Q1;
            {var subQ0=sQuery(id+"F52.wireOp",EDGE,"E150");Q1=makeQuery(id+"F52.imprint","IMPRINT",FACE,{"disambiguationData":[TD([[makeQuery(id+"F52.imprint","IMPRINT",EDGE,{"derivedFrom":subQ0}),1.0]])]});}
            extrude(context, id + "F53", {"entities" : qUnion([Q0, Q1]), "depth" : 5 * mm});
        }
        {
            var Q0;
            Q0=makeQuery(id+"F53.opExtrude","SWEPT_BODY",BODY,{"disambiguationData":[OSD([sQuery(id+"F52.wireOp",EDGE,"E148"),sQuery(id+"F52.wireOp",EDGE,"E149"),sQuery(id+"F52.wireOp",EDGE,"E150"),sQuery(id+"F52.wireOp",EDGE,"E151")])]});
            transform(context, id + "F54", {"entities" : qUnion([Q0]), "transformType" : TransformType.TRANSLATION_3D, "dx" : 0 * mm, "dy" : 155 * mm, "dz" : 0 * mm, "makeCopy" : true});
        }
        {
            var Q0;
            Q0=makeQuery(id+"F40.opExtrude","SWEPT_BODY",BODY,{"disambiguationData":[OSD([sQuery(id+"F39.wireOp",EDGE,"E92.bottom"),sQuery(id+"F39.wireOp",EDGE,"E92.left"),sQuery(id+"F39.wireOp",EDGE,"E92.right"),sQuery(id+"F39.wireOp",EDGE,"E93.trimOffspring"),sQuery(id+"F39.wireOp",EDGE,"E94.trimOffspring"),sQuery(id+"F39.wireOp",EDGE,"E97")])]});
            transform(context, id + "F55", {"entities" : qUnion([Q0]), "transformType" : TransformType.TRANSLATION_3D, "dx" : -211 * mm, "dy" : 0 * mm, "dz" : 0 * mm, "makeCopy" : true});
        }
        {
            var Q0;
            Q0=makeQuery(id+"F55.opPattern","COPY",FACE,{"derivedFrom":makeQuery(id+"F40.opExtrude","CAP_FACE",FACE,{"disambiguationData":[OSD([sQuery(id+"F39.wireOp",EDGE,"E92.bottom"),sQuery(id+"F39.wireOp",EDGE,"E92.left"),sQuery(id+"F39.wireOp",EDGE,"E92.right"),sQuery(id+"F39.wireOp",EDGE,"E93.trimOffspring"),sQuery(id+"F39.wireOp",EDGE,"E94.trimOffspring"),sQuery(id+"F39.wireOp",EDGE,"E97")])],"isStart":true}),"instanceName":"1"});
            var sketch = newSketch(context, id + "F56", { "sketchPlane" : qUnion([Q0])});
            skLineSegment(sketch, "E152", {"start": v(0, 92) * mm, "end": v(0, 6) * mm, "construction": true});
            skPoint(sketch, "E152.endSnap0", {"position": v(0, 13.36) * mm});
            skArc(sketch, "E153", {"start": v(-67.12, 53.25) * mm, "mid": v(0, 14.5) * mm, "end": v(67.12, 53.25) * mm});
            skArc(sketch, "E154", {"start": v(-53.26, 61.25) * mm, "mid": v(0, 30.5) * mm, "end": v(53.26, 61.25) * mm});
            skLineSegment(sketch, "E155", {"start": v(-67.12, 53.25) * mm, "end": v(-53.26, 61.25) * mm});
            skLineSegment(sketch, "E156", {"start": v(53.26, 61.25) * mm, "end": v(67.12, 53.25) * mm});
            skLineSegment(sketch, "E157", {"start": v(0, 14.5) * mm, "end": v(0, 30.5) * mm, "construction": true});
            skLineSegment(sketch, "E158", {"start": v(0, 0) * mm, "end": v(0, 14.5) * mm, "construction": true});
            skLineSegment(sketch, "E159", {"start": v(-39.69, 61.59) * mm, "end": v(-49.71, 55.8) * mm});
            skLineSegment(sketch, "E160", {"start": v(39.69, 61.59) * mm, "end": v(49.71, 55.8) * mm});
            skArc(sketch, "E161", {"start": v(-49.71, 55.8) * mm, "mid": v(0, 30.5) * mm, "end": v(49.71, 55.8) * mm});
            skArc(sketch, "E162", {"start": v(-39.69, 61.59) * mm, "mid": v(0, 42) * mm, "end": v(39.69, 61.59) * mm});
            skLineSegment(sketch, "E163", {"start": v(0, 92) * mm, "end": v(0, 30.5) * mm, "construction": true});
            skSolve(sketch);
        }
        {
            var Q0;
            Q0=makeQuery(id+"F56.imprint","IMPRINT",FACE,{"disambiguationData":[TD([[makeQuery(id+"F56.imprint","IMPRINT",EDGE,{"derivedFrom":sQuery(id+"F56.wireOp",EDGE,"E153")}),1.0]])]});
            extrude(context, id + "F57", {"entities" : qUnion([Q0]), "oppositeDirection" : true, "depth" : 19.5 * mm});
        }
        {
            var Q0;
            Q0=makeQuery(id+"F56.imprint","IMPRINT",FACE,{"disambiguationData":[TD([[makeQuery(id+"F56.imprint","IMPRINT",EDGE,{"derivedFrom":sQuery(id+"F56.wireOp",EDGE,"E159")}),1.0]])]});
            extrude(context, id + "F58", {"entities" : qUnion([Q0]), "oppositeDirection" : true, "depth" : 17.5 * mm});
        }
        {
            var Q0;
            Q0=makeQuery(id+"F55.opPattern","COPY",FACE,{"derivedFrom":makeQuery(id+"F40.opExtrude","CAP_FACE",FACE,{"disambiguationData":[OSD([sQuery(id+"F39.wireOp",EDGE,"E92.bottom"),sQuery(id+"F39.wireOp",EDGE,"E92.left"),sQuery(id+"F39.wireOp",EDGE,"E92.right"),sQuery(id+"F39.wireOp",EDGE,"E93.trimOffspring"),sQuery(id+"F39.wireOp",EDGE,"E94.trimOffspring"),sQuery(id+"F39.wireOp",EDGE,"E97")])],"isStart":true}),"instanceName":"1"});
            cPlane(context, id + "F59", {"entities" : qUnion([Q0]), "cplaneType" : CPlaneType.OFFSET, "offset" : 49 * mm, "oppositeDirection" : true, "width" : 150 * mm, "height" : 150 * mm});
        }
        {
            var Q0;
            Q0=qCreatedBy(id+"F59.planeOp",FACE);
            var sketch = newSketch(context, id + "F60", { "sketchPlane" : qUnion([Q0])});
            skCircle(sketch, "E164.0", {"center": v(0, 97) * mm, "radius": 10 * mm, "construction": true});
            skLineSegment(sketch, "E165.0", {"start": v(75, 6) * mm, "end": v(-75, 6) * mm});
            skLineSegment(sketch, "E166", {"start": v(0, 97) * mm, "end": v(0, 6) * mm, "construction": true});
            skCircle(sketch, "E167", {"center": v(0, 97) * mm, "radius": 68.5 * mm});
            skLineSegment(sketch, "E168", {"start": v(0, 97) * mm, "end": v(50, 50.18) * mm});
            skLineSegment(sketch, "E169", {"start": v(50, 50.18) * mm, "end": v(50, 6) * mm});
            skLineSegment(sketch, "E170", {"start": v(-50, 50.18) * mm, "end": v(-50, 6) * mm});
            skCircle(sketch, "E171", {"center": v(0, 97) * mm, "radius": 52.5 * mm});
            skLineSegment(sketch, "E172", {"start": v(0, 97) * mm, "end": v(-50, 50.18) * mm});
            skCircle(sketch, "E173", {"center": v(0, 97) * mm, "radius": 43.5 * mm});
            skSolve(sketch);
        }
        {
            var Q0;
            {var subQ0=sQuery(id+"F60.wireOp",EDGE,"E169");Q0=makeQuery(id+"F60.imprint","IMPRINT",FACE,{"disambiguationData":[TD([[makeQuery(id+"F60.imprint","IMPRINT",EDGE,{"derivedFrom":subQ0}),-1.0]])]});}
            extrude(context, id + "F61", {"entities" : qUnion([Q0]), "depth" : 25 * mm});
        }
        {
            var Q0;
            {var subQ0=sQuery(id+"F60.wireOp",EDGE,"E168");var subQ5=sQuery(id+"F60.wireOp",EDGE,"E171");var subQ6=makeQuery(id+"F60.imprint","INTERSECT",VERTEX,{"derivedFrom":[subQ0,subQ5]});Q0=makeQuery(id+"F60.imprint","IMPRINT",FACE,{"disambiguationData":[TD([[makeQuery(id+"F60.imprint","IMPRINT",EDGE,{"disambiguationData":[TD([[subQ6,1.0]])],"derivedFrom":subQ5}),-1.0]])]});}
            extrude(context, id + "F62", {"entities" : qUnion([Q0]), "depth" : 25 * mm});
        }
        {
            var Q0;
            {var subQ0=sQuery(id+"F60.wireOp",EDGE,"E173");var subQ1=sQuery(id+"F60.wireOp",EDGE,"E168");var subQ2=makeQuery(id+"F60.imprint","INTERSECT",VERTEX,{"derivedFrom":[subQ1,subQ0]});Q0=makeQuery(id+"F60.imprint","IMPRINT",FACE,{"disambiguationData":[TD([[makeQuery(id+"F60.imprint","IMPRINT",EDGE,{"disambiguationData":[TD([[subQ2,-1.0]])],"derivedFrom":subQ1}),-1.0]])]});}
            extrude(context, id + "F63", {"entities" : qUnion([Q0]), "depth" : 25 * mm});
        }
        {
            var Q0;
            Q0=makeQuery(id+"F1.opExtrude","CAP_FACE",FACE,{"disambiguationData":[OSD([sQuery(id+"F0.wireOp",EDGE,"E0.right"),sQuery(id+"F0.wireOp",EDGE,"E2"),sQuery(id+"F0.wireOp",EDGE,"E3"),sQuery(id+"F0.wireOp",EDGE,"E4"),sQuery(id+"F0.wireOp",EDGE,"E5"),sQuery(id+"F0.wireOp",EDGE,"E6"),sQuery(id+"F0.wireOp",EDGE,"E8"),sQuery(id+"F0.wireOp",EDGE,"E9"),sQuery(id+"F0.wireOp",EDGE,"E10"),sQuery(id+"F0.wireOp",EDGE,"E13"),sQuery(id+"F0.wireOp",EDGE,"E14"),sQuery(id+"F0.wireOp",EDGE,"E15"),sQuery(id+"F0.wireOp",EDGE,"E16"),sQuery(id+"F0.wireOp",EDGE,"E17"),sQuery(id+"F0.wireOp",EDGE,"E18"),sQuery(id+"F0.wireOp",EDGE,"E19"),sQuery(id+"F0.wireOp",EDGE,"E21"),sQuery(id+"F0.wireOp",EDGE,"E22"),sQuery(id+"F0.wireOp",EDGE,"E23"),sQuery(id+"F0.wireOp",EDGE,"E24"),sQuery(id+"F0.wireOp",EDGE,"E25"),sQuery(id+"F0.wireOp",EDGE,"E26"),sQuery(id+"F0.wireOp",EDGE,"E27"),sQuery(id+"F0.wireOp",EDGE,"E28"),sQuery(id+"F0.wireOp",EDGE,"E29"),sQuery(id+"F0.wireOp",EDGE,"E30")])],"isStart":true});
            var sketch = newSketch(context, id + "F64", { "sketchPlane" : qUnion([Q0])});
            skLineSegment(sketch, "E174.0", {"start": v(-5, 50) * mm, "end": v(-30, 50) * mm, "construction": true});
            skLineSegment(sketch, "E175.0", {"start": v(-5, -50) * mm, "end": v(-30, -50) * mm, "construction": true});
            skLineSegment(sketch, "E176", {"start": v(-17.5, 50) * mm, "end": v(-17.5, -50) * mm, "construction": true});
            skLineSegment(sketch, "E177", {"start": v(-17.5, 0) * mm, "end": v(-39.07, 0) * mm, "construction": true});
            skPoint(sketch, "E177.endSnap0", {"position": v(-17.5, 0) * mm});
            skCircle(sketch, "E178", {"center": v(-17.5, -25) * mm, "radius": 3 * mm});
            skCircle(sketch, "E179", {"center": v(-17.5, 25) * mm, "radius": 3 * mm});
            skLineSegment(sketch, "E180", {"start": v(-320, 68) * mm, "end": v(-288, 100) * mm, "construction": true});
            skCircle(sketch, "E181", {"center": v(-304, 84) * mm, "radius": 15 * mm, "construction": true});
            skCircle(sketch, "E182", {"center": v(-304, 84) * mm, "radius": 4.25 * mm});
            skCircle(sketch, "E183", {"center": v(-304, -84) * mm, "radius": 4.25 * mm});
            skLineSegment(sketch, "E184", {"start": v(198, 210) * mm, "end": v(230, 178) * mm, "construction": true});
            skCircle(sketch, "E185", {"center": v(214, 194) * mm, "radius": 4.25 * mm});
            skCircle(sketch, "E186", {"center": v(214, -194) * mm, "radius": 4.25 * mm});
            skSolve(sketch);
        }
        {
            var Q0;
            Q0=makeQuery(id+"F64.imprint","IMPRINT",FACE,{"disambiguationData":[TD([[makeQuery(id+"F64.imprint","IMPRINT",EDGE,{"derivedFrom":sQuery(id+"F64.wireOp",EDGE,"E179")}),1.0]])]});
            var Q1;
            Q1=makeQuery(id+"F64.imprint","IMPRINT",FACE,{"disambiguationData":[TD([[makeQuery(id+"F64.imprint","IMPRINT",EDGE,{"derivedFrom":sQuery(id+"F64.wireOp",EDGE,"E178")}),1.0]])]});
            extrude(context, id + "F65", {"entities" : qUnion([Q0, Q1]), "operationType" : NewBodyOperationType.REMOVE, "endBound" : BoundingType.THROUGH_ALL, "oppositeDirection" : true, "depth" : 70 * mm});
        }
        {
            var Q0;
            Q0=makeQuery(id+"F64.imprint","IMPRINT",FACE,{"disambiguationData":[TD([[makeQuery(id+"F64.imprint","IMPRINT",EDGE,{"derivedFrom":sQuery(id+"F64.wireOp",EDGE,"E182")}),1.0]])]});
            var Q1;
            Q1=makeQuery(id+"F64.imprint","IMPRINT",FACE,{"disambiguationData":[TD([[makeQuery(id+"F64.imprint","IMPRINT",EDGE,{"derivedFrom":sQuery(id+"F64.wireOp",EDGE,"E183")}),1.0]])]});
            var Q2;
            Q2=makeQuery(id+"F64.imprint","IMPRINT",FACE,{"disambiguationData":[TD([[makeQuery(id+"F64.imprint","IMPRINT",EDGE,{"derivedFrom":sQuery(id+"F64.wireOp",EDGE,"E186")}),1.0]])]});
            var Q3;
            Q3=makeQuery(id+"F64.imprint","IMPRINT",FACE,{"disambiguationData":[TD([[makeQuery(id+"F64.imprint","IMPRINT",EDGE,{"derivedFrom":sQuery(id+"F64.wireOp",EDGE,"E185")}),1.0]])]});
            extrude(context, id + "F66", {"entities" : qUnion([Q0, Q1, Q2, Q3]), "operationType" : NewBodyOperationType.REMOVE, "oppositeDirection" : true, "depth" : 25 * mm});
        }
    });
